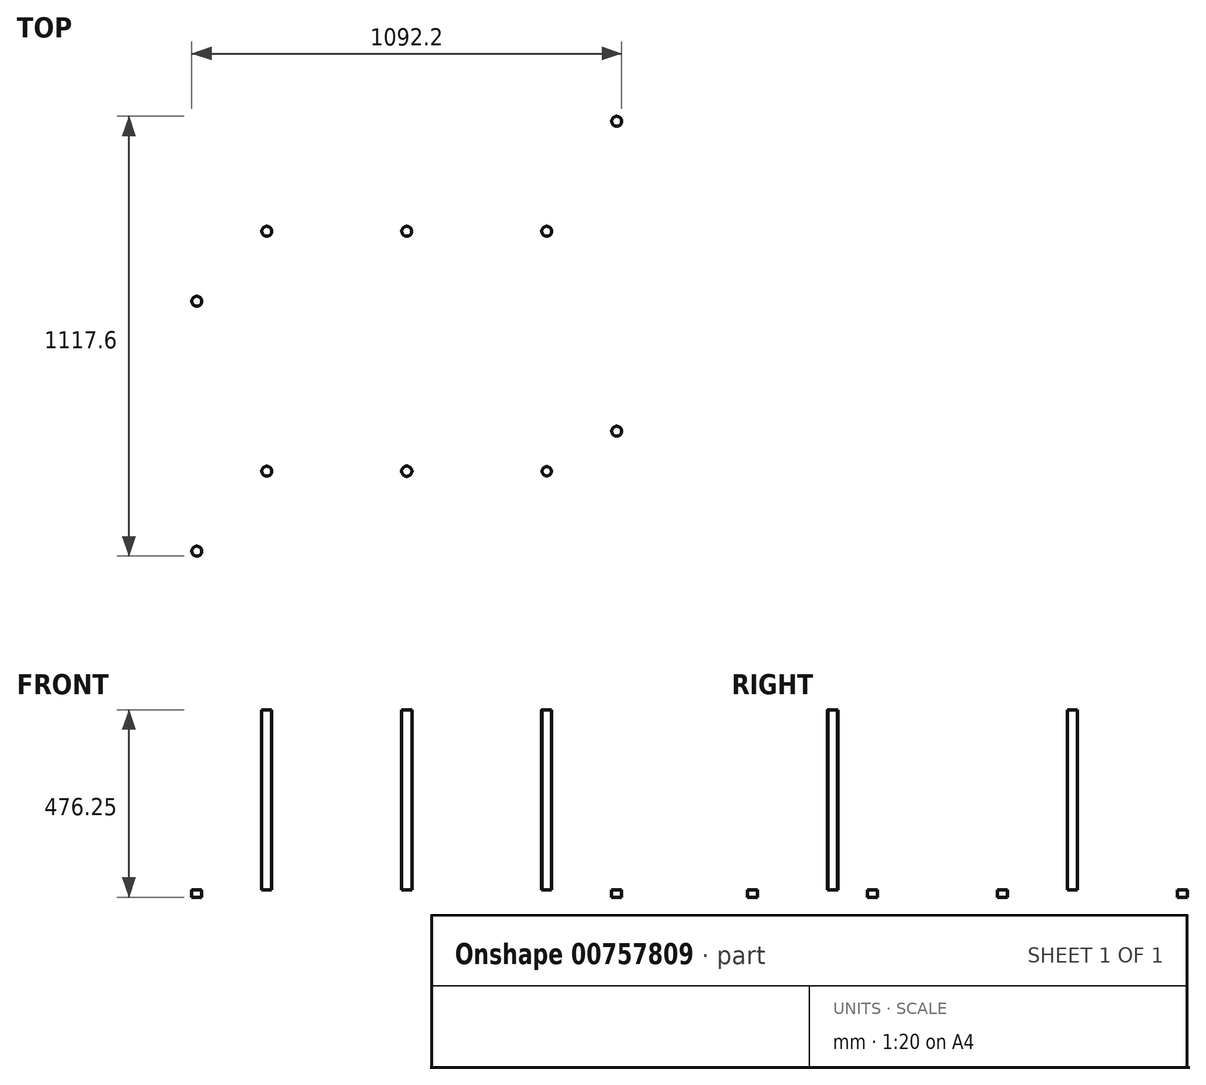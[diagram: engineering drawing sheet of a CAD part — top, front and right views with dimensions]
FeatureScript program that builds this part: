
annotation { "Feature Type Name" : "Feature", "Feature Type Description" : "" }
export const myFeature = defineFeature(function(context is Context, id is Id, definition is map)
    precondition{}
    {
        {
            var Q0;
            Q0=qCreatedBy(makeId("Top.planeOp"),FACE);
            var sketch = newSketch(context, id + "F0", { "sketchPlane" : qUnion([Q0])});
            skLineSegment(sketch, "E0.bottom", {"start": v(558.8, -304.8) * mm, "end": v(-558.8, -304.8) * mm});
            skLineSegment(sketch, "E0.top", {"start": v(558.8, 304.8) * mm, "end": v(-558.8, 304.8) * mm});
            skLineSegment(sketch, "E0.left", {"start": v(558.8, -304.8) * mm, "end": v(558.8, 304.8) * mm});
            skLineSegment(sketch, "E0.right", {"start": v(-558.8, -304.8) * mm, "end": v(-558.8, 304.8) * mm});
            skPoint(sketch, "E0.middle", {"position": v(0, 0) * mm});
            skSolve(sketch);
        }
        {
            var Q0;
            Q0=makeQuery(id+"F0.imprint","IMPRINT",FACE,{"disambiguationData":[TD([[makeQuery(id+"F0.imprint","IMPRINT",EDGE,{"derivedFrom":sQuery(id+"F0.wireOp",EDGE,"E0.bottom")}),-1.0]])]});
            extrude(context, id + "F1", {"entities" : qUnion([Q0]), "depth" : 19.05 * mm, "offsetDistance" : 25.4 * mm});
        }
        {
            var Q0;
            Q0=makeQuery(id+"F1.opExtrude","CAP_FACE",FACE,{"disambiguationData":[OSD([sQuery(id+"F0.wireOp",EDGE,"E0.bottom"),sQuery(id+"F0.wireOp",EDGE,"E0.top"),sQuery(id+"F0.wireOp",EDGE,"E0.left"),sQuery(id+"F0.wireOp",EDGE,"E0.right")])],"isStart":false});
            var sketch = newSketch(context, id + "F2", { "sketchPlane" : qUnion([Q0])});
            skLineSegment(sketch, "E1.bottom", {"start": v(558.8, -838.2) * mm, "end": v(-558.8, -838.2) * mm});
            skLineSegment(sketch, "E1.top", {"start": v(558.8, -381) * mm, "end": v(-558.8, -381) * mm});
            skLineSegment(sketch, "E1.left", {"start": v(558.8, -838.2) * mm, "end": v(558.8, -381) * mm});
            skLineSegment(sketch, "E1.right", {"start": v(-558.8, -838.2) * mm, "end": v(-558.8, -381) * mm});
            skPoint(sketch, "E1.middle", {"position": v(0, -609.6) * mm});
            skSolve(sketch);
        }
        {
            var Q0;
            Q0=makeQuery(id+"F2.imprint","IMPRINT",FACE,{"disambiguationData":[TD([[makeQuery(id+"F2.imprint","IMPRINT",EDGE,{"derivedFrom":sQuery(id+"F2.wireOp",EDGE,"E1.bottom")}),-1.0]])]});
            extrude(context, id + "F3", {"entities" : qUnion([Q0]), "oppositeDirection" : true, "depth" : 19.05 * mm, "offsetDistance" : 25.4 * mm});
        }
        {
            var Q0;
            Q0=makeQuery(id+"F1.opExtrude","CAP_FACE",FACE,{"disambiguationData":[OSD([sQuery(id+"F0.wireOp",EDGE,"E0.bottom"),sQuery(id+"F0.wireOp",EDGE,"E0.top"),sQuery(id+"F0.wireOp",EDGE,"E0.left"),sQuery(id+"F0.wireOp",EDGE,"E0.right")])],"isStart":false});
            var sketch = newSketch(context, id + "F4", { "sketchPlane" : qUnion([Q0])});
            skCircle(sketch, "E2", {"center": v(-533.4, 279.4) * mm, "radius": 12.7 * mm});
            skCircle(sketch, "E3.MirrorC", {"center": v(533.4, 279.4) * mm, "radius": 12.7 * mm});
            skCircle(sketch, "E4.MirrorC", {"center": v(-533.4, -177.8) * mm, "radius": 12.7 * mm});
            skCircle(sketch, "E5.MirrorC", {"center": v(533.4, -177.8) * mm, "radius": 12.7 * mm});
            skSolve(sketch);
        }
        {
            var Q0;
            Q0=makeQuery(id+"F3.opExtrude","CAP_FACE",FACE,{"disambiguationData":[OSD([sQuery(id+"F2.wireOp",EDGE,"E1.bottom"),sQuery(id+"F2.wireOp",EDGE,"E1.top"),sQuery(id+"F2.wireOp",EDGE,"E1.left"),sQuery(id+"F2.wireOp",EDGE,"E1.right")])],"isStart":true});
            var sketch = newSketch(context, id + "F5", { "sketchPlane" : qUnion([Q0])});
            skCircle(sketch, "E6", {"center": v(-533.4, -508) * mm, "radius": 12.7 * mm});
            skLineSegment(sketch, "E7", {"start": v(-558.8, -609.6) * mm, "end": v(558.8, -609.6) * mm, "construction": true});
            skLineSegment(sketch, "E8", {"start": v(0, -381) * mm, "end": v(0, -838.2) * mm, "construction": true});
            skCircle(sketch, "E9.MirrorC", {"center": v(533.4, -508) * mm, "radius": 12.7 * mm});
            skCircle(sketch, "E10.MirrorC", {"center": v(-533.4, -812.8) * mm, "radius": 12.7 * mm});
            skCircle(sketch, "E11.MirrorC", {"center": v(533.4, -812.8) * mm, "radius": 12.7 * mm});
            skSolve(sketch);
        }
        {
            var Q0;
            Q0=makeQuery(id+"F4.imprint","IMPRINT",FACE,{"disambiguationData":[TD([[makeQuery(id+"F4.imprint","IMPRINT",EDGE,{"derivedFrom":sQuery(id+"F4.wireOp",EDGE,"E3.MirrorC")}),-1.0]])]});
            var Q1;
            Q1=makeQuery(id+"F4.imprint","IMPRINT",FACE,{"disambiguationData":[TD([[makeQuery(id+"F4.imprint","IMPRINT",EDGE,{"derivedFrom":sQuery(id+"F4.wireOp",EDGE,"E5.MirrorC")}),1.0]])]});
            var Q2;
            Q2=makeQuery(id+"F4.imprint","IMPRINT",FACE,{"disambiguationData":[TD([[makeQuery(id+"F4.imprint","IMPRINT",EDGE,{"derivedFrom":sQuery(id+"F4.wireOp",EDGE,"E4.MirrorC")}),-1.0]])]});
            var Q3;
            Q3=makeQuery(id+"F4.imprint","IMPRINT",FACE,{"disambiguationData":[TD([[makeQuery(id+"F4.imprint","IMPRINT",EDGE,{"derivedFrom":sQuery(id+"F4.wireOp",EDGE,"E2")}),1.0]])]});
            extrude(context, id + "F6", {"entities" : qUnion([Q0, Q1, Q2, Q3]), "operationType" : NewBodyOperationType.REMOVE, "oppositeDirection" : true, "depth" : 25.4 * mm, "offsetDistance" : 25.4 * mm});
        }
        {
            var Q0;
            Q0=makeQuery(id+"F5.imprint","IMPRINT",FACE,{"disambiguationData":[TD([[makeQuery(id+"F5.imprint","IMPRINT",EDGE,{"derivedFrom":sQuery(id+"F5.wireOp",EDGE,"E6")}),1.0]])]});
            var Q1;
            Q1=makeQuery(id+"F5.imprint","IMPRINT",FACE,{"disambiguationData":[TD([[makeQuery(id+"F5.imprint","IMPRINT",EDGE,{"derivedFrom":sQuery(id+"F5.wireOp",EDGE,"E10.MirrorC")}),-1.0]])]});
            var Q2;
            Q2=makeQuery(id+"F5.imprint","IMPRINT",FACE,{"disambiguationData":[TD([[makeQuery(id+"F5.imprint","IMPRINT",EDGE,{"derivedFrom":sQuery(id+"F5.wireOp",EDGE,"E11.MirrorC")}),1.0]])]});
            var Q3;
            Q3=makeQuery(id+"F5.imprint","IMPRINT",FACE,{"disambiguationData":[TD([[makeQuery(id+"F5.imprint","IMPRINT",EDGE,{"derivedFrom":sQuery(id+"F5.wireOp",EDGE,"E9.MirrorC")}),-1.0]])]});
            extrude(context, id + "F7", {"entities" : qUnion([Q0, Q1, Q2, Q3]), "operationType" : NewBodyOperationType.REMOVE, "oppositeDirection" : true, "depth" : 25.4 * mm, "offsetDistance" : 25.4 * mm});
        }
        {
            var Q0;
            Q0=makeQuery(id+"F1.opExtrude","CAP_FACE",FACE,{"disambiguationData":[OSD([sQuery(id+"F0.wireOp",EDGE,"E0.bottom"),sQuery(id+"F0.wireOp",EDGE,"E0.top"),sQuery(id+"F0.wireOp",EDGE,"E0.left"),sQuery(id+"F0.wireOp",EDGE,"E0.right")])],"isStart":false});
            var sketch = newSketch(context, id + "F8", { "sketchPlane" : qUnion([Q0])});
            skCircle(sketch, "E12", {"center": v(-355.6, 0) * mm, "radius": 12.7 * mm});
            skPoint(sketch, "E12.centerSnap0", {"position": v(-558.8, 0) * mm});
            skCircle(sketch, "E13", {"center": v(0, 0) * mm, "radius": 12.7 * mm});
            skCircle(sketch, "E14", {"center": v(355.6, 0) * mm, "radius": 12.7 * mm});
            skSolve(sketch);
        }
        {
            var Q0;
            Q0=makeQuery(id+"F8.imprint","IMPRINT",FACE,{"disambiguationData":[TD([[makeQuery(id+"F8.imprint","IMPRINT",EDGE,{"derivedFrom":sQuery(id+"F8.wireOp",EDGE,"E12")}),1.0]])]});
            var Q1;
            Q1=makeQuery(id+"F8.imprint","IMPRINT",FACE,{"disambiguationData":[TD([[makeQuery(id+"F8.imprint","IMPRINT",EDGE,{"derivedFrom":sQuery(id+"F8.wireOp",EDGE,"E13")}),1.0]])]});
            var Q2;
            Q2=makeQuery(id+"F8.imprint","IMPRINT",FACE,{"disambiguationData":[TD([[makeQuery(id+"F8.imprint","IMPRINT",EDGE,{"derivedFrom":sQuery(id+"F8.wireOp",EDGE,"E14")}),1.0]])]});
            extrude(context, id + "F9", {"entities" : qUnion([Q0, Q1, Q2]), "operationType" : NewBodyOperationType.ADD, "depth" : 457.2 * mm, "offsetDistance" : 25.4 * mm});
        }
        {
            var Q0;
            Q0=makeQuery(id+"F3.opExtrude","CAP_FACE",FACE,{"disambiguationData":[OSD([sQuery(id+"F2.wireOp",EDGE,"E1.bottom"),sQuery(id+"F2.wireOp",EDGE,"E1.top"),sQuery(id+"F2.wireOp",EDGE,"E1.left"),sQuery(id+"F2.wireOp",EDGE,"E1.right")])],"isStart":true});
            var sketch = newSketch(context, id + "F10", { "sketchPlane" : qUnion([Q0])});
            skCircle(sketch, "E15", {"center": v(-355.6, -609.6) * mm, "radius": 12.7 * mm});
            skCircle(sketch, "E16", {"center": v(0, -609.6) * mm, "radius": 12.96 * mm});
            skCircle(sketch, "E17", {"center": v(355.6, -609.6) * mm, "radius": 11.73 * mm});
            skSolve(sketch);
        }
        {
            var Q0;
            Q0=makeQuery(id+"F10.imprint","IMPRINT",FACE,{"disambiguationData":[TD([[makeQuery(id+"F10.imprint","IMPRINT",EDGE,{"derivedFrom":sQuery(id+"F10.wireOp",EDGE,"E15")}),1.0]])]});
            var Q1;
            Q1=makeQuery(id+"F10.imprint","IMPRINT",FACE,{"disambiguationData":[TD([[makeQuery(id+"F10.imprint","IMPRINT",EDGE,{"derivedFrom":sQuery(id+"F10.wireOp",EDGE,"E17")}),1.0]])]});
            var Q2;
            Q2=makeQuery(id+"F10.imprint","IMPRINT",FACE,{"disambiguationData":[TD([[makeQuery(id+"F10.imprint","IMPRINT",EDGE,{"derivedFrom":sQuery(id+"F10.wireOp",EDGE,"E16")}),1.0]])]});
            extrude(context, id + "F11", {"entities" : qUnion([Q0, Q1, Q2]), "operationType" : NewBodyOperationType.ADD, "depth" : 457.2 * mm, "offsetDistance" : 25.4 * mm});
        }
    });
